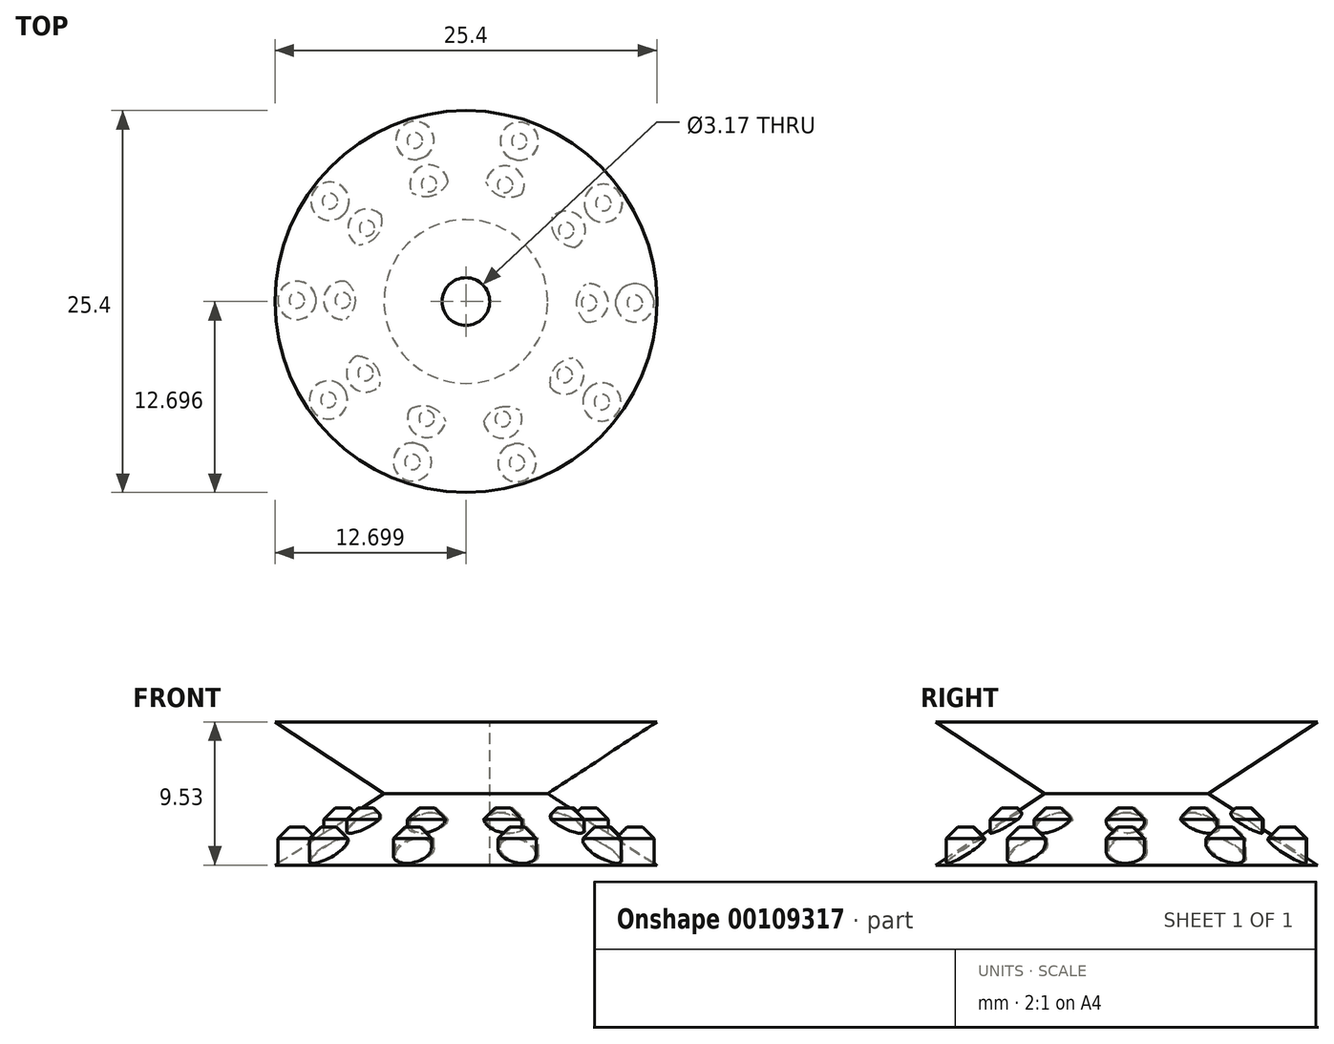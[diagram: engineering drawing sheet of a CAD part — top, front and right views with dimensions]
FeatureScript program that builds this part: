
annotation { "Feature Type Name" : "Feature", "Feature Type Description" : "" }
export const myFeature = defineFeature(function(context is Context, id is Id, definition is map)
    precondition{}
    {
        {
            var Q0;
            Q0=qCreatedBy(makeId("Top.planeOp"),FACE);
            var sketch = newSketch(context, id + "F0", { "sketchPlane" : qUnion([Q0])});
            skCircle(sketch, "E0", {"center": v(-15.24, 5.24) * mm, "radius": 12.7 * mm});
            skSolve(sketch);
        }
        {
            var Q0;
            Q0=makeQuery(id+"F0.imprint","IMPRINT",FACE,{"disambiguationData":[TD([[makeQuery(id+"F0.imprint","IMPRINT",EDGE,{"derivedFrom":sQuery(id+"F0.wireOp",EDGE,"E0")}),1.0]])]});
            cPlane(context, id + "F1", {"entities" : qUnion([Q0]), "cplaneType" : CPlaneType.OFFSET, "offset" : 4.76 * mm, "width" : 152.4 * mm, "height" : 152.4 * mm});
        }
        {
            var Q0;
            Q0=qCreatedBy(id+"F1.planeOp",FACE);
            var sketch = newSketch(context, id + "F2", { "sketchPlane" : qUnion([Q0])});
            skCircle(sketch, "E1", {"center": v(-15.24, 5.24) * mm, "radius": 5.45 * mm});
            skSolve(sketch);
        }
        {
            var Q0;
            Q0=makeQuery(id+"F0.imprint","IMPRINT",FACE,{"disambiguationData":[TD([[makeQuery(id+"F0.imprint","IMPRINT",EDGE,{"derivedFrom":sQuery(id+"F0.wireOp",EDGE,"E0")}),1.0]])]});
            var Q1;
            Q1=makeQuery(id+"F2.imprint","IMPRINT",FACE,{"disambiguationData":[TD([[makeQuery(id+"F2.imprint","IMPRINT",EDGE,{"derivedFrom":sQuery(id+"F2.wireOp",EDGE,"E1")}),1.0]])]});
            loft(context, id + "F3", {"sheetProfilesArray" : [{ "sheetProfileEntities" : qUnion([Q0]) }, { "sheetProfileEntities" : qUnion([Q1]) }]});
        }
        {
            var Q0;
            Q0=makeQuery(id+"F3.opLoft","CAP_FACE",FACE,{"disambiguationData":[OSD([makeQuery(id+"F0.imprint","IMPRINT",FACE,{"disambiguationData":[TD([[makeQuery(id+"F0.imprint","IMPRINT",EDGE,{"derivedFrom":sQuery(id+"F0.wireOp",EDGE,"E0")}),1.0]])]})])],"isStart":true});
            cPlane(context, id + "F4", {"entities" : qUnion([Q0]), "cplaneType" : CPlaneType.OFFSET, "offset" : 1.27 * mm, "oppositeDirection" : true, "width" : 152.4 * mm, "height" : 152.4 * mm});
        }
        {
            var Q0;
            Q0=qCreatedBy(id+"F4.planeOp",FACE);
            var sketch = newSketch(context, id + "F5", { "sketchPlane" : qUnion([Q0])});
            skCircle(sketch, "E2", {"center": v(-4, -5.15) * mm, "radius": 1.27 * mm});
            skSolve(sketch);
        }
        {
            var Q0;
            Q0=makeQuery(id+"F5.imprint","IMPRINT",FACE,{"disambiguationData":[TD([[makeQuery(id+"F5.imprint","IMPRINT",EDGE,{"derivedFrom":sQuery(id+"F5.wireOp",EDGE,"E2")}),1.0]])]});
            extrude(context, id + "F6", {"entities" : qUnion([Q0]), "depth" : 2.54 * mm, "symmetric" : true});
        }
        {
            var Q0;
            Q0=makeQuery(id+"F6.opExtrude","CAP_EDGE",EDGE,{"disambiguationData":[OSD([sQuery(id+"F5.wireOp",EDGE,"E2")])],"isStart":true});
            chamfer(context, id + "F7", {"entities" : qUnion([Q0]), "width" : 0.76 * mm, "tangentPropagation" : true});
        }
        {
            var Q0;
            Q0=makeQuery(id+"F3.opLoft","CAP_FACE",FACE,{"disambiguationData":[OSD([makeQuery(id+"F2.imprint","IMPRINT",FACE,{"disambiguationData":[TD([[makeQuery(id+"F2.imprint","IMPRINT",EDGE,{"derivedFrom":sQuery(id+"F2.wireOp",EDGE,"E1")}),1.0]])]})])],"isStart":true});
            var sketch = newSketch(context, id + "F8", { "sketchPlane" : qUnion([Q0])});
            skLineSegment(sketch, "E3", {"start": v(-15.24, 5.24) * mm, "end": v(-9.8, 5.24) * mm, "construction": true});
            skSolve(sketch);
        }
        {
            var Q0;
            Q0=qCreatedBy(id+"F4.planeOp",FACE);
            cPlane(context, id + "F9", {"entities" : qUnion([Q0]), "cplaneType" : CPlaneType.OFFSET, "offset" : 2.54 * mm, "oppositeDirection" : true, "width" : 152.4 * mm, "height" : 152.4 * mm});
        }
        {
            var Q0;
            Q0=qCreatedBy(id+"F9.planeOp",FACE);
            var sketch = newSketch(context, id + "F10", { "sketchPlane" : qUnion([Q0])});
            skCircle(sketch, "E4", {"center": v(-7.05, -5.15) * mm, "radius": 1.27 * mm});
            skSolve(sketch);
        }
        {
            var Q0;
            Q0=makeQuery(id+"F10.imprint","IMPRINT",FACE,{"disambiguationData":[TD([[makeQuery(id+"F10.imprint","IMPRINT",EDGE,{"derivedFrom":sQuery(id+"F10.wireOp",EDGE,"E4")}),1.0]])]});
            extrude(context, id + "F11", {"entities" : qUnion([Q0]), "depth" : 1.78 * mm});
        }
        {
            var Q0;
            Q0=makeQuery(id+"F11.opExtrude","CAP_EDGE",EDGE,{"disambiguationData":[OSD([sQuery(id+"F10.wireOp",EDGE,"E4")])],"isStart":true});
            chamfer(context, id + "F12", {"entities" : qUnion([Q0]), "width" : 0.76 * mm, "tangentPropagation" : true});
        }
        {
            var Q0;
            Q0=makeQuery(id+"F6.opExtrude","SWEPT_BODY",BODY,{"disambiguationData":[OSD([sQuery(id+"F5.wireOp",EDGE,"E2")])]});
            var Q1;
            Q1=makeQuery(id+"F11.opExtrude","SWEPT_BODY",BODY,{"disambiguationData":[OSD([sQuery(id+"F10.wireOp",EDGE,"E4")])]});
            var Q2;
            Q2=makeQuery(id+"F3.opLoft","SWEPT_FACE",FACE,{"disambiguationData":[OSD([sQuery(id+"F0.wireOp",EDGE,"E0"),sQuery(id+"F2.wireOp",EDGE,"E1")])]});
            circularPattern(context, id + "F13", {"entities" : qUnion([Q0, Q1]), "axis" : qUnion([Q2]), "angle" : 360 * degree, "instanceCount" : 10, "equalSpace" : true});
        }
        {
            var Q0;
            Q0=makeQuery(id+"F8.imprint","IMPRINT",FACE,{"disambiguationData":[TD([[makeQuery(id+"F8.imprint","IMPRINT",EDGE,{"derivedFrom":makeQuery(id+"F3.opLoft","MID_CAP_EDGE",EDGE,{"disambiguationData":[OSD([sQuery(id+"F0.wireOp",EDGE,"E0"),sQuery(id+"F2.wireOp",EDGE,"E1")])],"capPos":1.0})}),1.0]])]});
            var sketch = newSketch(context, id + "F14", { "sketchPlane" : qUnion([Q0])});
            skCircle(sketch, "E5.0.0", {"center": v(-15.24, 5.24) * mm, "radius": 5.45 * mm, "construction": true});
            skCircle(sketch, "E6", {"center": v(-15.24, 5.24) * mm, "radius": 1.59 * mm});
            skSolve(sketch);
        }
        {
            var Q0;
            Q0=makeQuery(id+"F14.imprint","IMPRINT",FACE,{"disambiguationData":[TD([[makeQuery(id+"F14.imprint","IMPRINT",EDGE,{"derivedFrom":sQuery(id+"F14.wireOp",EDGE,"E6")}),1.0]])]});
            extrude(context, id + "F15", {"entities" : qUnion([Q0]), "operationType" : NewBodyOperationType.REMOVE, "endBound" : BoundingType.THROUGH_ALL, "oppositeDirection" : true, "depth" : 25.4 * mm});
        }
        {
            var Q0;
            Q0=makeQuery(id+"F3.opLoft","SWEPT_BODY",BODY,{"disambiguationData":[OSD([makeQuery(id+"F0.imprint","IMPRINT",FACE,{"disambiguationData":[TD([[makeQuery(id+"F0.imprint","IMPRINT",EDGE,{"derivedFrom":sQuery(id+"F0.wireOp",EDGE,"E0")}),1.0]])]}),makeQuery(id+"F2.imprint","IMPRINT",FACE,{"disambiguationData":[TD([[makeQuery(id+"F2.imprint","IMPRINT",EDGE,{"derivedFrom":sQuery(id+"F2.wireOp",EDGE,"E1")}),1.0]])]})])]});
            var Q1;
            Q1=makeQuery(id+"F8.imprint","IMPRINT",FACE,{"disambiguationData":[TD([[makeQuery(id+"F8.imprint","IMPRINT",EDGE,{"derivedFrom":makeQuery(id+"F3.opLoft","MID_CAP_EDGE",EDGE,{"disambiguationData":[OSD([sQuery(id+"F0.wireOp",EDGE,"E0"),sQuery(id+"F2.wireOp",EDGE,"E1")])],"capPos":1.0})}),1.0]])]});
            mirror(context, id + "F16", {"operationType" : NewBodyOperationType.ADD, "entities" : qUnion([Q0]), "mirrorPlane" : qUnion([Q1])});
        }
    });
